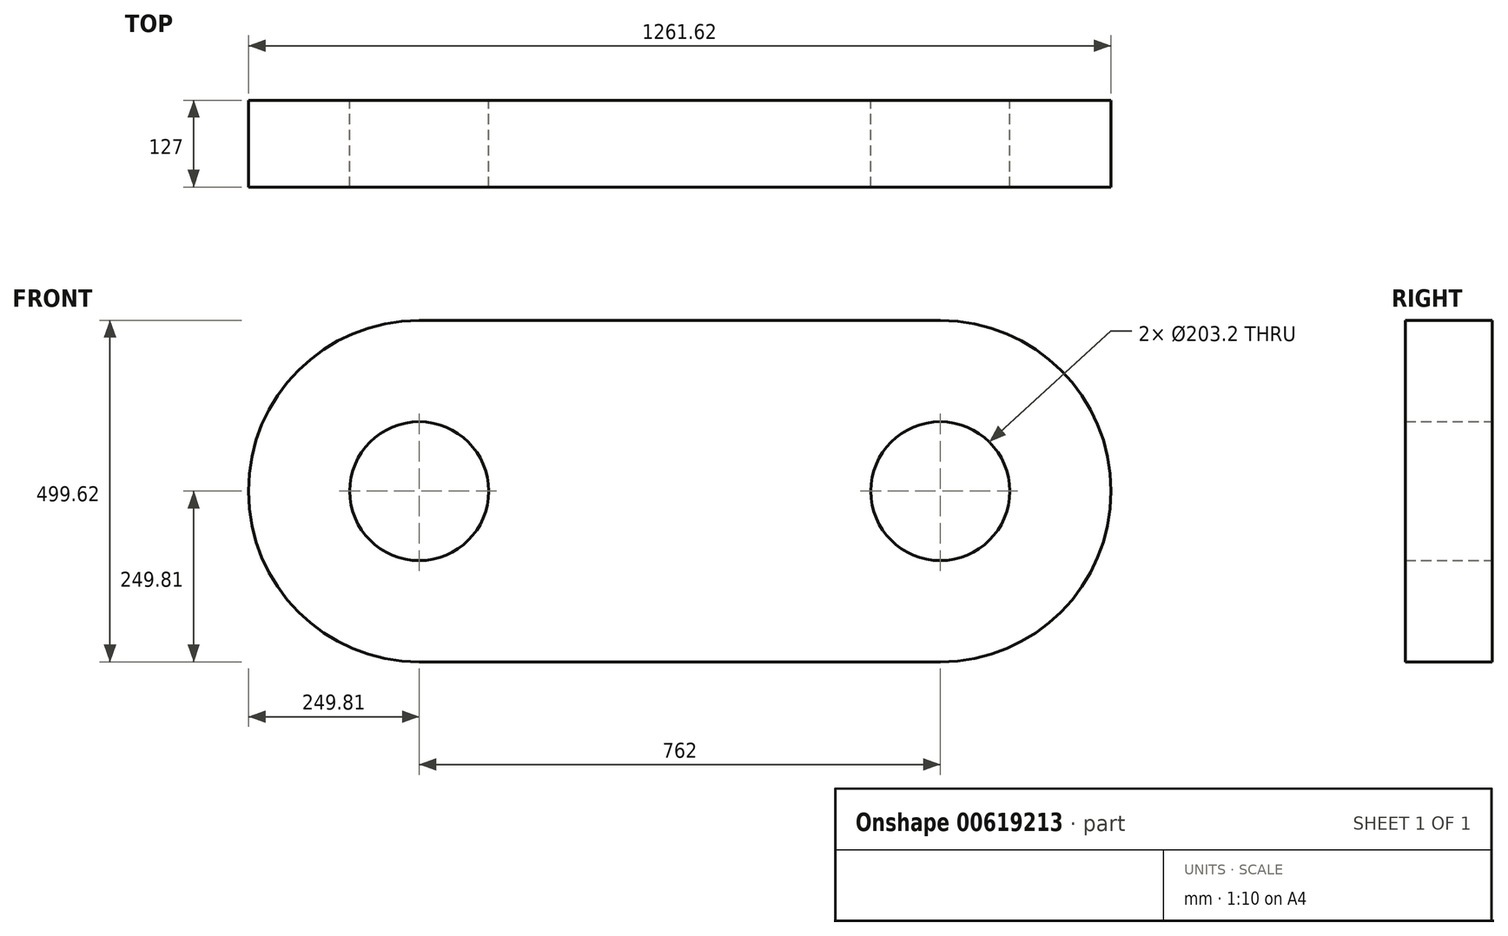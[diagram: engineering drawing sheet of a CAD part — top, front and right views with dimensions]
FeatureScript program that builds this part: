
annotation { "Feature Type Name" : "Feature", "Feature Type Description" : "" }
export const myFeature = defineFeature(function(context is Context, id is Id, definition is map)
    precondition{}
    {
        {
            var Q0;
            Q0=qCreatedBy(makeId("Front.planeOp"),FACE);
            var sketch = newSketch(context, id + "F0", { "sketchPlane" : qUnion([Q0])});
            skArc(sketch, "E0", {"start": v(0, -249.8) * mm, "mid": v(249.8, 0) * mm, "end": v(0, 249.8) * mm});
            skArc(sketch, "E1", {"start": v(-762, 249.8) * mm, "mid": v(-1011.8, 0) * mm, "end": v(-762, -249.8) * mm});
            skLineSegment(sketch, "E2", {"start": v(-762, 249.8) * mm, "end": v(0, 249.8) * mm});
            skLineSegment(sketch, "E3", {"start": v(-762, -249.8) * mm, "end": v(0, -249.8) * mm});
            skCircle(sketch, "E4", {"center": v(-762, 0) * mm, "radius": 101.6 * mm});
            skCircle(sketch, "E5", {"center": v(0, 0) * mm, "radius": 101.6 * mm});
            skSolve(sketch);
        }
        {
            var Q0;
            Q0=makeQuery(id+"F0.imprint","IMPRINT",FACE,{"disambiguationData":[TD([[makeQuery(id+"F0.imprint","IMPRINT",EDGE,{"derivedFrom":sQuery(id+"F0.wireOp",EDGE,"E0")}),1.0]])]});
            extrude(context, id + "F1", {"entities" : qUnion([Q0]), "depth" : 127 * mm, "offsetDistance" : 25.4 * mm});
        }
    });
